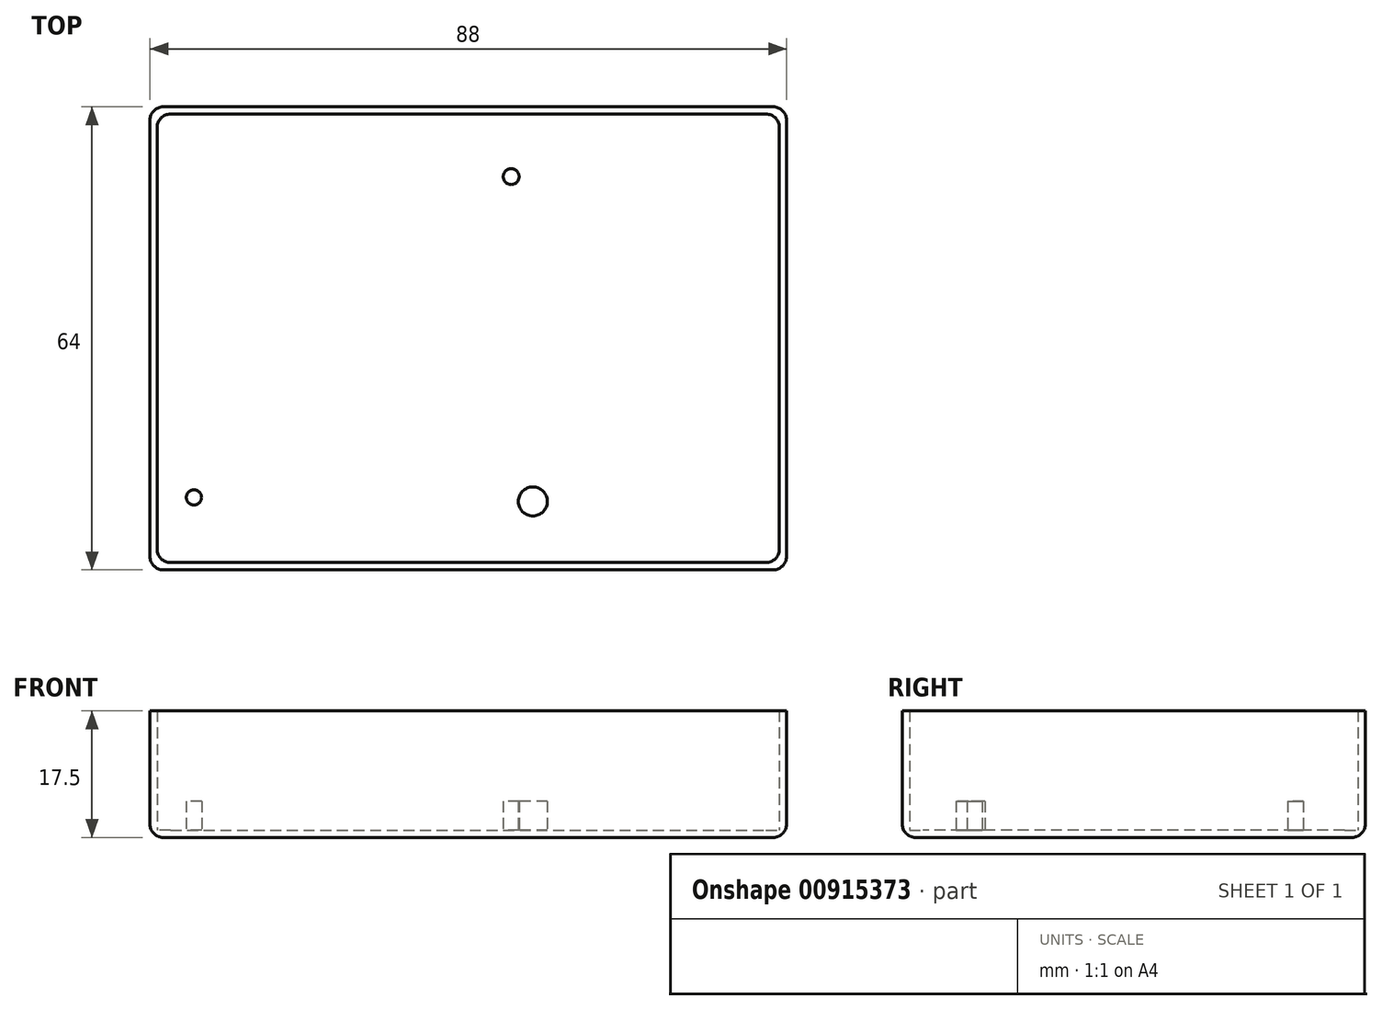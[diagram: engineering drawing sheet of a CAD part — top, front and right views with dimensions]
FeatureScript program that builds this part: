
annotation { "Feature Type Name" : "Feature", "Feature Type Description" : "" }
export const myFeature = defineFeature(function(context is Context, id is Id, definition is map)
    precondition{}
    {
        {
            var Q0;
            Q0=qCreatedBy(makeId("Top.planeOp"),FACE);
            var sketch = newSketch(context, id + "F0", { "sketchPlane" : qUnion([Q0])});
            skLineSegment(sketch, "E0.bottom", {"start": v(-43, 31) * mm, "end": v(43, 31) * mm});
            skLineSegment(sketch, "E0.top", {"start": v(-43, -31) * mm, "end": v(43, -31) * mm});
            skLineSegment(sketch, "E0.left", {"start": v(-43, 31) * mm, "end": v(-43, -31) * mm});
            skLineSegment(sketch, "E0.right", {"start": v(43, 31) * mm, "end": v(43, -31) * mm});
            skLineSegment(sketch, "E1.bottom", {"start": v(-40.97, 28.45) * mm, "end": v(12.03, 28.45) * mm});
            skLineSegment(sketch, "E1.top", {"start": v(-40.97, -28.55) * mm, "end": v(12.03, -28.55) * mm});
            skLineSegment(sketch, "E1.left", {"start": v(-40.97, 28.45) * mm, "end": v(-40.97, -28.55) * mm});
            skLineSegment(sketch, "E1.right", {"start": v(12.03, 28.45) * mm, "end": v(12.03, -28.55) * mm});
            skLineSegment(sketch, "E2.bottom", {"start": v(15.33, 25.4) * mm, "end": v(41.33, 25.4) * mm});
            skLineSegment(sketch, "E2.top", {"start": v(15.33, -26.6) * mm, "end": v(41.33, -26.6) * mm});
            skLineSegment(sketch, "E2.left", {"start": v(15.33, 25.4) * mm, "end": v(15.33, -26.6) * mm});
            skLineSegment(sketch, "E2.right", {"start": v(41.33, 25.4) * mm, "end": v(41.33, -26.6) * mm});
            skCircle(sketch, "E3", {"center": v(5.93, 22.35) * mm, "radius": 1.1 * mm});
            skCircle(sketch, "E4", {"center": v(8.93, -22.55) * mm, "radius": 2 * mm});
            skCircle(sketch, "E5", {"center": v(-37.92, -22) * mm, "radius": 1.05 * mm});
            skLineSegment(sketch, "E6.bottom", {"start": v(-44, 32) * mm, "end": v(44, 32) * mm});
            skLineSegment(sketch, "E6.top", {"start": v(-44, -32) * mm, "end": v(44, -32) * mm});
            skLineSegment(sketch, "E6.left", {"start": v(-44, 32) * mm, "end": v(-44, -32) * mm});
            skLineSegment(sketch, "E6.right", {"start": v(44, 32) * mm, "end": v(44, -32) * mm});
            skSolve(sketch);
        }
        {
            var Q0;
            Q0=makeQuery(id+"F0.imprint","IMPRINT",FACE,{"disambiguationData":[TD([[makeQuery(id+"F0.imprint","IMPRINT",EDGE,{"derivedFrom":sQuery(id+"F0.wireOp",EDGE,"E0.bottom")}),1.0]])]});
            extrude(context, id + "F1", {"entities" : qUnion([Q0]), "depth" : 17.5 * mm, "offsetDistance" : 25.4 * mm});
        }
        {
            var Q0;
            Q0=makeQuery(id+"F0.imprint","IMPRINT",FACE,{"disambiguationData":[TD([[makeQuery(id+"F0.imprint","IMPRINT",EDGE,{"derivedFrom":sQuery(id+"F0.wireOp",EDGE,"E1.bottom")}),-1.0]])]});
            var Q1;
            Q1=makeQuery(id+"F0.imprint","IMPRINT",FACE,{"disambiguationData":[TD([[makeQuery(id+"F0.imprint","IMPRINT",EDGE,{"derivedFrom":sQuery(id+"F0.wireOp",EDGE,"E2.bottom")}),-1.0]])]});
            var Q2;
            Q2=makeQuery(id+"F0.imprint","IMPRINT",FACE,{"disambiguationData":[TD([[makeQuery(id+"F0.imprint","IMPRINT",EDGE,{"derivedFrom":sQuery(id+"F0.wireOp",EDGE,"E0.bottom")}),-1.0]])]});
            extrude(context, id + "F2", {"entities" : qUnion([Q0, Q1, Q2]), "operationType" : NewBodyOperationType.ADD, "depth" : 1 * mm, "offsetDistance" : 25.4 * mm});
        }
        {
            var Q0;
            Q0=makeQuery(id+"F0.imprint","IMPRINT",FACE,{"disambiguationData":[TD([[makeQuery(id+"F0.imprint","IMPRINT",EDGE,{"derivedFrom":sQuery(id+"F0.wireOp",EDGE,"E4")}),1.0]])]});
            var Q1;
            Q1=makeQuery(id+"F0.imprint","IMPRINT",FACE,{"disambiguationData":[TD([[makeQuery(id+"F0.imprint","IMPRINT",EDGE,{"derivedFrom":sQuery(id+"F0.wireOp",EDGE,"E5")}),1.0]])]});
            var Q2;
            Q2=makeQuery(id+"F0.imprint","IMPRINT",FACE,{"disambiguationData":[TD([[makeQuery(id+"F0.imprint","IMPRINT",EDGE,{"derivedFrom":sQuery(id+"F0.wireOp",EDGE,"E3")}),1.0]])]});
            extrude(context, id + "F3", {"entities" : qUnion([Q0, Q1, Q2]), "operationType" : NewBodyOperationType.ADD, "depth" : 5 * mm, "offsetDistance" : 25.4 * mm});
        }
        {
            var Q0;
            Q0=makeQuery(id+"F1.opExtrude","SWEPT_EDGE",EDGE,{"disambiguationData":[OSD([sQuery(id+"F0.wireOp",EDGE,"E6.top"),sQuery(id+"F0.wireOp",EDGE,"E6.left")])]});
            var Q1;
            Q1=makeQuery(id+"F1.opExtrude","SWEPT_EDGE",EDGE,{"disambiguationData":[OSD([sQuery(id+"F0.wireOp",EDGE,"E6.top"),sQuery(id+"F0.wireOp",EDGE,"E6.right")])]});
            var Q2;
            Q2=makeQuery(id+"F1.opExtrude","SWEPT_EDGE",EDGE,{"disambiguationData":[OSD([sQuery(id+"F0.wireOp",EDGE,"E6.bottom"),sQuery(id+"F0.wireOp",EDGE,"E6.right")])]});
            var Q3;
            Q3=makeQuery(id+"F1.opExtrude","SWEPT_EDGE",EDGE,{"disambiguationData":[OSD([sQuery(id+"F0.wireOp",EDGE,"E6.bottom"),sQuery(id+"F0.wireOp",EDGE,"E6.left")])]});
            var Q4;
            Q4=makeQuery(id+"F1.opExtrude","CAP_EDGE",EDGE,{"disambiguationData":[OSD([sQuery(id+"F0.wireOp",EDGE,"E6.top")])],"isStart":true});
            var Q5;
            Q5=makeQuery(id+"F1.opExtrude","CAP_EDGE",EDGE,{"disambiguationData":[OSD([sQuery(id+"F0.wireOp",EDGE,"E6.left")])],"isStart":true});
            var Q6;
            Q6=makeQuery(id+"F1.opExtrude","CAP_EDGE",EDGE,{"disambiguationData":[OSD([sQuery(id+"F0.wireOp",EDGE,"E6.bottom")])],"isStart":true});
            var Q7;
            Q7=makeQuery(id+"F1.opExtrude","CAP_EDGE",EDGE,{"disambiguationData":[OSD([sQuery(id+"F0.wireOp",EDGE,"E6.right")])],"isStart":true});
            var Q8;
            Q8=makeQuery(id+"F1.opExtrude","SWEPT_EDGE",EDGE,{"disambiguationData":[OSD([sQuery(id+"F0.wireOp",EDGE,"E0.top"),sQuery(id+"F0.wireOp",EDGE,"E0.left")])]});
            var Q9;
            Q9=makeQuery(id+"F1.opExtrude","SWEPT_EDGE",EDGE,{"disambiguationData":[OSD([sQuery(id+"F0.wireOp",EDGE,"E0.bottom"),sQuery(id+"F0.wireOp",EDGE,"E0.left")])]});
            var Q10;
            Q10=makeQuery(id+"F1.opExtrude","SWEPT_EDGE",EDGE,{"disambiguationData":[OSD([sQuery(id+"F0.wireOp",EDGE,"E0.bottom"),sQuery(id+"F0.wireOp",EDGE,"E0.right")])]});
            var Q11;
            Q11=makeQuery(id+"F1.opExtrude","SWEPT_EDGE",EDGE,{"disambiguationData":[OSD([sQuery(id+"F0.wireOp",EDGE,"E0.top"),sQuery(id+"F0.wireOp",EDGE,"E0.right")])]});
            fillet(context, id + "F4", {"entities" : qUnion([Q0, Q1, Q2, Q3, Q4, Q5, Q6, Q7, Q8, Q9, Q10, Q11]), "radius" : 1.84 * mm, "tangentPropagation" : true, "allowEdgeOverflow" : false});
        }
    });
